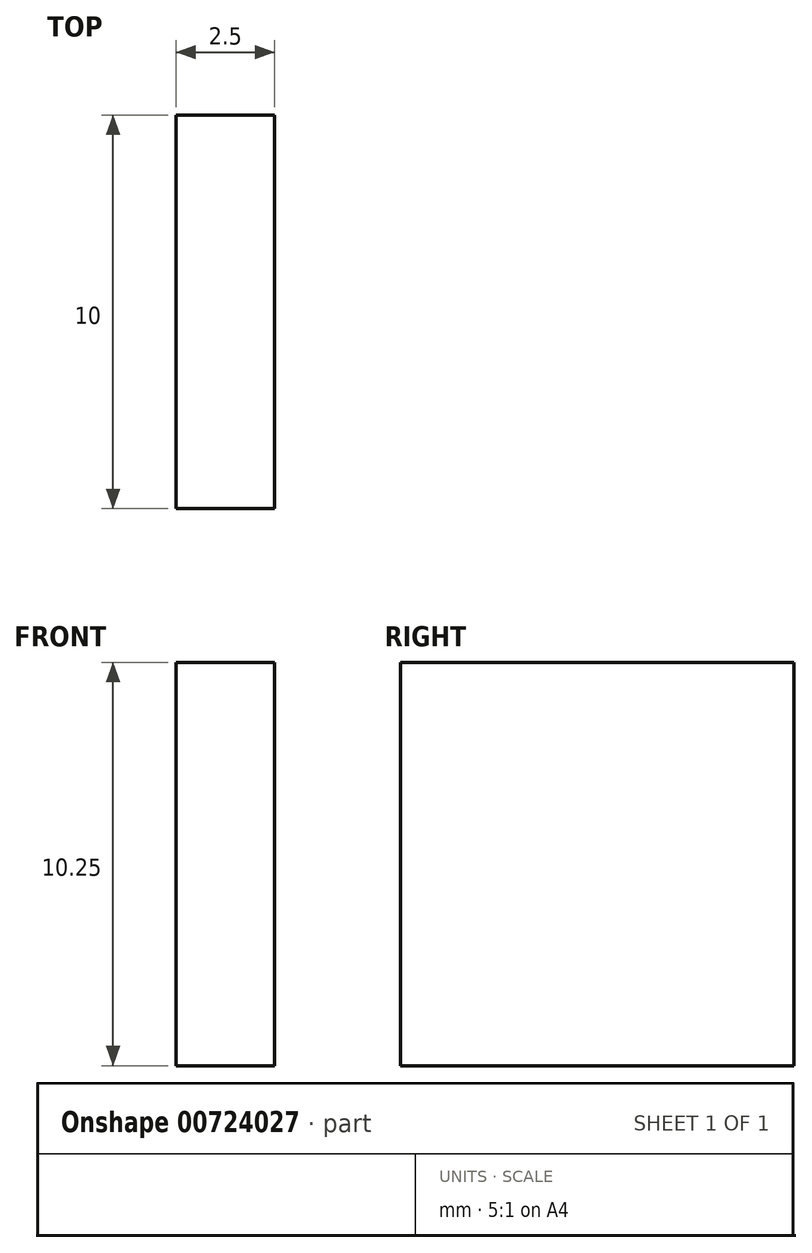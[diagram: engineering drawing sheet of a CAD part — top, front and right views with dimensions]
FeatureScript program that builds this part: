
annotation { "Feature Type Name" : "Feature", "Feature Type Description" : "" }
export const myFeature = defineFeature(function(context is Context, id is Id, definition is map)
    precondition{}
    {
        {
            var Q0;
            Q0=qCreatedBy(makeId("Right.planeOp"),FACE);
            var sketch = newSketch(context, id + "F0", { "sketchPlane" : qUnion([Q0])});
            skLineSegment(sketch, "E0.bottom", {"start": v(0, 0) * mm, "end": v(10, 0) * mm});
            skLineSegment(sketch, "E0.top", {"start": v(0, -10.25) * mm, "end": v(10, -10.25) * mm});
            skLineSegment(sketch, "E0.left", {"start": v(0, 0) * mm, "end": v(0, -10.25) * mm});
            skLineSegment(sketch, "E0.right", {"start": v(10, 0) * mm, "end": v(10, -10.25) * mm});
            skSolve(sketch);
        }
        {
            var Q0;
            Q0=makeQuery(id+"F0.imprint","IMPRINT",FACE,{"disambiguationData":[TD([[makeQuery(id+"F0.imprint","IMPRINT",EDGE,{"derivedFrom":sQuery(id+"F0.wireOp",EDGE,"E0.bottom")}),-1.0]])]});
            extrude(context, id + "F1", {"entities" : qUnion([Q0]), "depth" : 2.5 * mm, "offsetDistance" : 25 * mm});
        }
    });
